# Revit family: Hager-Orion_Plus-IP65-D300-Cl.II-Poly_double_encl-630A-NoHosted-FR-fr
name_source: partatom
category: Electrical Equipment
units: mm (PartAtom-declared; Revit-internal decimal feet)

## family parameters
Always vertical = Yes
Cut with Voids When Loaded = No
Panel Configuration = Two Columns, Circuits Across
Part Type = Panelboard
Room Calculation Point = No
Round Connector Dimension = Use Diameter
Shared = No
Work Plane-Based = Yes

## types (1)
- saillie IP65 L850 H1450 P300  - FL352B
    Default Elevation = 1219 mm
    EF000003 - mode de pose = EV000384 - saillie
    EF000007 - couleur = EV000270 - gris
    EF000008 - largeur = 850 mm  [stored 2.78871 ft]
    EF000040 - hauteur = 1450 mm  [stored 4.75722 ft]
    EF000049 - profondeur = 300 mm  [stored 0.984252 ft]
    EF000116 - numéro RAL = 7035
    EF000118 - avec cadre/support de montage = Yes
    EF000218 - profondeur d'encastrement = 0 mm  [stored 0 ft]
    EF000266 - nombre de rangées = 3
    EF000339 - type de capot = EV001012 - couvercle
    EF000437 - nombre d'entrées de conduit = 0
    EF001088 - possibilité de montage en saillie = No
    EF001131 - profondeur intérieure = 300 mm  [stored 0.984252 ft]
    EF001596 - matériau du boîtier/corps = EV000139 - plastique
    EF001613 - maintien de fonction = EV000494 - sans
    EF002950 - largeur en nombre de modules = 0
    EF003532 - convient pour utilisation à l’extérieur = No
    EF004293 - indice de protection contre les chocs (IK) = EV006814 - IK08
    EF004427 - nombre de modules = 111
    EF004464 - type de porte = EV002646 - unique
    EF005474 - indice de protection (IP) = EV006421 - IP65
    EF006244 - couvercle/porte transparent(e) = No
    EF006306 - avec serrure = Yes
    EF007800 - adapté à un parafoudre = No
    EF008873 - courant nominal (In) = 630 A
    EF009170 - épaisseur de matériau du boîtier = 2 mm  [stored 0.00656168 ft]
    EF009171 - épaisseur de matériau de la porte/du couvercle = 2 mm  [stored 0.00656168 ft]
    EF009212 - finition du couvercle = EV000116 - fermé
    EF009554 - nombre d'ouvertures pour plaques à bride = 0
    EF015940 - couvercle avec décharge de pression = No
    HG000002 - avec porte = Yes
    HG000003 - Gamme = Orion Plus
    HG000004 - Référence fabricant = FL352B
    HG000006 - Encastré = No
    HG000009 - Porte à double battant = No
    HG000010 - Portes asymétriques = No
    HG000023 - Armoire double section = Yes
    HG000024 - Hauteur de la section basse = 600 mm
    HG000026 - Installation au sol = No
    HG000027 - Hauteur du socle = 70 mm  [stored 0.229659 ft]
    Manufacturer = Hager
    Type Comments = Orion Plus

note: [stored X ft] marks values corroborated as IEEE doubles in the binary element streams (Revit-internal decimal feet)

## geometry (parser evidence)
native form markers: Blend x4, Sweep x5
no freeform markers — native parametric forms only
